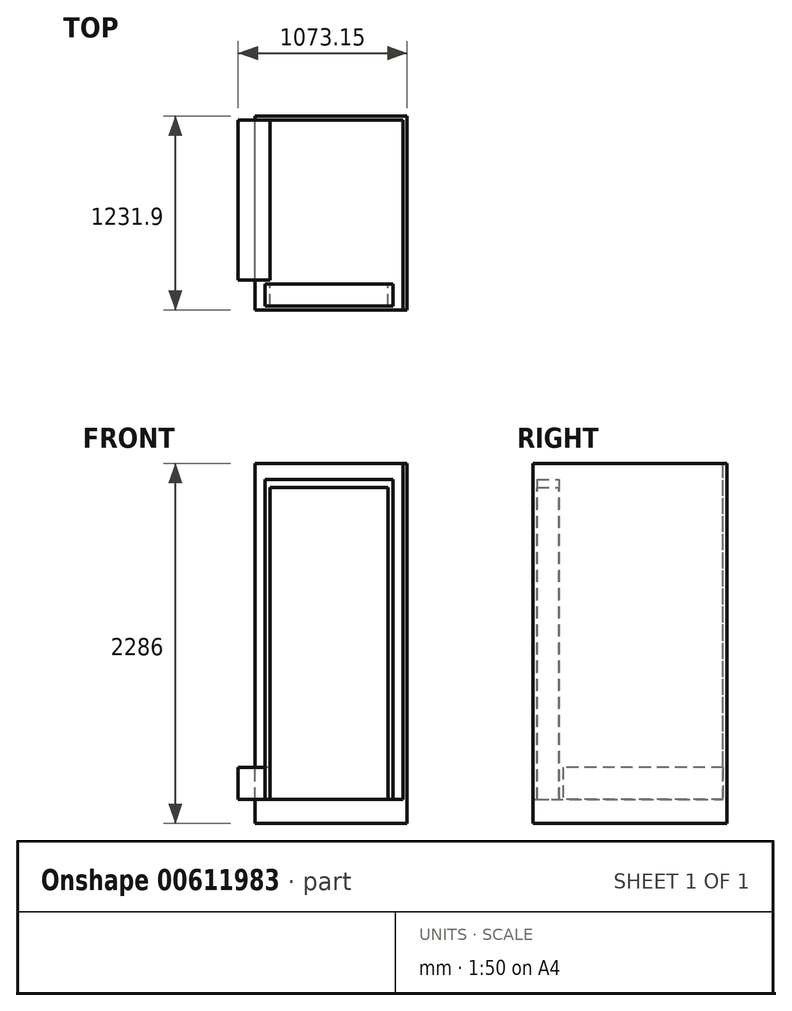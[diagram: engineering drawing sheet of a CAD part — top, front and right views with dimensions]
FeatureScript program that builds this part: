
annotation { "Feature Type Name" : "Feature", "Feature Type Description" : "" }
export const myFeature = defineFeature(function(context is Context, id is Id, definition is map)
    precondition{}
    {
        {
            var Q0;
            Q0=qCreatedBy(makeId("Front.planeOp"),FACE);
            var sketch = newSketch(context, id + "F0", { "sketchPlane" : qUnion([Q0])});
            skLineSegment(sketch, "E0.top", {"start": v(-374.65, 1981.2) * mm, "end": v(374.65, 1981.2) * mm});
            skLineSegment(sketch, "E0.left", {"start": v(-374.65, 0) * mm, "end": v(-374.65, 1981.2) * mm});
            skLineSegment(sketch, "E0.right", {"start": v(374.65, 0) * mm, "end": v(374.65, 1981.2) * mm});
            skLineSegment(sketch, "E1.bottom", {"start": v(406.4, 2032) * mm, "end": v(-406.4, 2032) * mm});
            skLineSegment(sketch, "E1.top", {"start": v(406.4, 0) * mm, "end": v(374.65, 0) * mm});
            skLineSegment(sketch, "E1.left", {"start": v(406.4, 2032) * mm, "end": v(406.4, 0) * mm});
            skLineSegment(sketch, "E1.right", {"start": v(-406.4, 2032) * mm, "end": v(-406.4, 0) * mm});
            skPoint(sketch, "E2", {"position": v(0, 1981.2) * mm});
            skPoint(sketch, "E3", {"position": v(0, 2032) * mm});
            skLineSegment(sketch, "E4.trimOffspring", {"start": v(-374.65, 0) * mm, "end": v(-406.4, 0) * mm});
            skSolve(sketch);
        }
        {
            var Q0;
            Q0 = qSketchRegion(id + "F0", true);
            extrude(context, id + "F1", {"entities" : qUnion([Q0]), "depth" : 139.7 * mm, "offsetDistance" : 25.4 * mm});
        }
        {
            var Q0;
            Q0=makeQuery(id+"F1.opExtrude","SWEPT_FACE",FACE,{"disambiguationData":[OSD([sQuery(id+"F0.wireOp",EDGE,"E4.trimOffspring")])]});
            var sketch = newSketch(context, id + "F2", { "sketchPlane" : qUnion([Q0])});
            skLineSegment(sketch, "E5.bottom", {"start": v(469.9, 165.1) * mm, "end": v(-469.9, 165.1) * mm});
            skLineSegment(sketch, "E5.top", {"start": v(469.9, -1041.4) * mm, "end": v(-469.9, -1041.4) * mm});
            skLineSegment(sketch, "E5.left", {"start": v(469.9, 165.1) * mm, "end": v(469.9, -1041.4) * mm});
            skLineSegment(sketch, "E5.right", {"start": v(-469.9, 165.1) * mm, "end": v(-469.9, -1041.4) * mm});
            skPoint(sketch, "E6", {"position": v(0, 165.1) * mm});
            skSolve(sketch);
        }
        {
            var Q0;
            Q0 = qSketchRegion(id + "F2", true);
            extrude(context, id + "F3", {"entities" : qUnion([Q0]), "operationType" : NewBodyOperationType.ADD, "depth" : 152.4 * mm, "offsetDistance" : 25.4 * mm});
        }
        {
            var Q0;
            Q0=makeQuery(id+"F3.opExtrude","SWEPT_FACE",FACE,{"disambiguationData":[OSD([sQuery(id+"F2.wireOp",EDGE,"E5.top")])]});
            var sketch = newSketch(context, id + "F4", { "sketchPlane" : qUnion([Q0])});
            skLineSegment(sketch, "E7.bottom", {"start": v(469.9, -152.4) * mm, "end": v(-469.9, -152.4) * mm});
            skLineSegment(sketch, "E7.top", {"start": v(469.9, 2133.6) * mm, "end": v(-469.9, 2133.6) * mm});
            skLineSegment(sketch, "E7.left", {"start": v(469.9, -152.4) * mm, "end": v(469.9, 2133.6) * mm});
            skLineSegment(sketch, "E7.right", {"start": v(-469.9, -152.4) * mm, "end": v(-469.9, 2133.6) * mm});
            skSolve(sketch);
        }
        {
            var Q0;
            Q0 = qSketchRegion(id + "F4", true);
            extrude(context, id + "F5", {"entities" : qUnion([Q0]), "operationType" : NewBodyOperationType.ADD, "depth" : 25.4 * mm, "offsetDistance" : 25.4 * mm});
        }
        {
            var Q0;
            Q0=makeQuery(id+"F5.boolean.opBoolean","MERGE",FACE,{"derivedFrom":[makeQuery(id+"F3.opExtrude","SWEPT_FACE",FACE,{"disambiguationData":[OSD([sQuery(id+"F2.wireOp",EDGE,"E5.left")])]}),makeQuery(id+"F5.opExtrude","SWEPT_FACE",FACE,{"disambiguationData":[OSD([sQuery(id+"F4.wireOp",EDGE,"E7.right")])]})]});
            var sketch = newSketch(context, id + "F6", { "sketchPlane" : qUnion([Q0])});
            skLineSegment(sketch, "E8.bottom", {"start": v(-165.1, -152.4) * mm, "end": v(1066.8, -152.4) * mm});
            skLineSegment(sketch, "E8.top", {"start": v(-165.1, 2133.6) * mm, "end": v(1066.8, 2133.6) * mm});
            skLineSegment(sketch, "E8.left", {"start": v(-165.1, -152.4) * mm, "end": v(-165.1, 2133.6) * mm});
            skLineSegment(sketch, "E8.right", {"start": v(1066.8, -152.4) * mm, "end": v(1066.8, 2133.6) * mm});
            skSolve(sketch);
        }
        {
            var Q0;
            Q0 = qSketchRegion(id + "F6", true);
            extrude(context, id + "F7", {"entities" : qUnion([Q0]), "operationType" : NewBodyOperationType.ADD, "depth" : 25.4 * mm, "offsetDistance" : 25.4 * mm});
        }
        {
            var Q0;
            Q0=makeQuery(id+"F3.opExtrude","CAP_FACE",FACE,{"disambiguationData":[OSD([sQuery(id+"F2.wireOp",EDGE,"E5.bottom"),sQuery(id+"F2.wireOp",EDGE,"E5.top"),sQuery(id+"F2.wireOp",EDGE,"E5.left"),sQuery(id+"F2.wireOp",EDGE,"E5.right")])],"isStart":true});
            var sketch = newSketch(context, id + "F8", { "sketchPlane" : qUnion([Q0])});
            skLineSegment(sketch, "E9.bottom", {"start": v(-374.65, 1041.4) * mm, "end": v(-577.85, 1041.4) * mm});
            skLineSegment(sketch, "E9.top", {"start": v(-374.65, 25.4) * mm, "end": v(-577.85, 25.4) * mm});
            skLineSegment(sketch, "E9.left", {"start": v(-374.65, 1041.4) * mm, "end": v(-374.65, 25.4) * mm});
            skLineSegment(sketch, "E9.right", {"start": v(-577.85, 1041.4) * mm, "end": v(-577.85, 25.4) * mm});
            skSolve(sketch);
        }
        {
            var Q0;
            Q0 = qSketchRegion(id + "F8", true);
            extrude(context, id + "F9", {"entities" : qUnion([Q0]), "operationType" : NewBodyOperationType.ADD, "depth" : 203.2 * mm, "offsetDistance" : 25.4 * mm});
        }
    });
